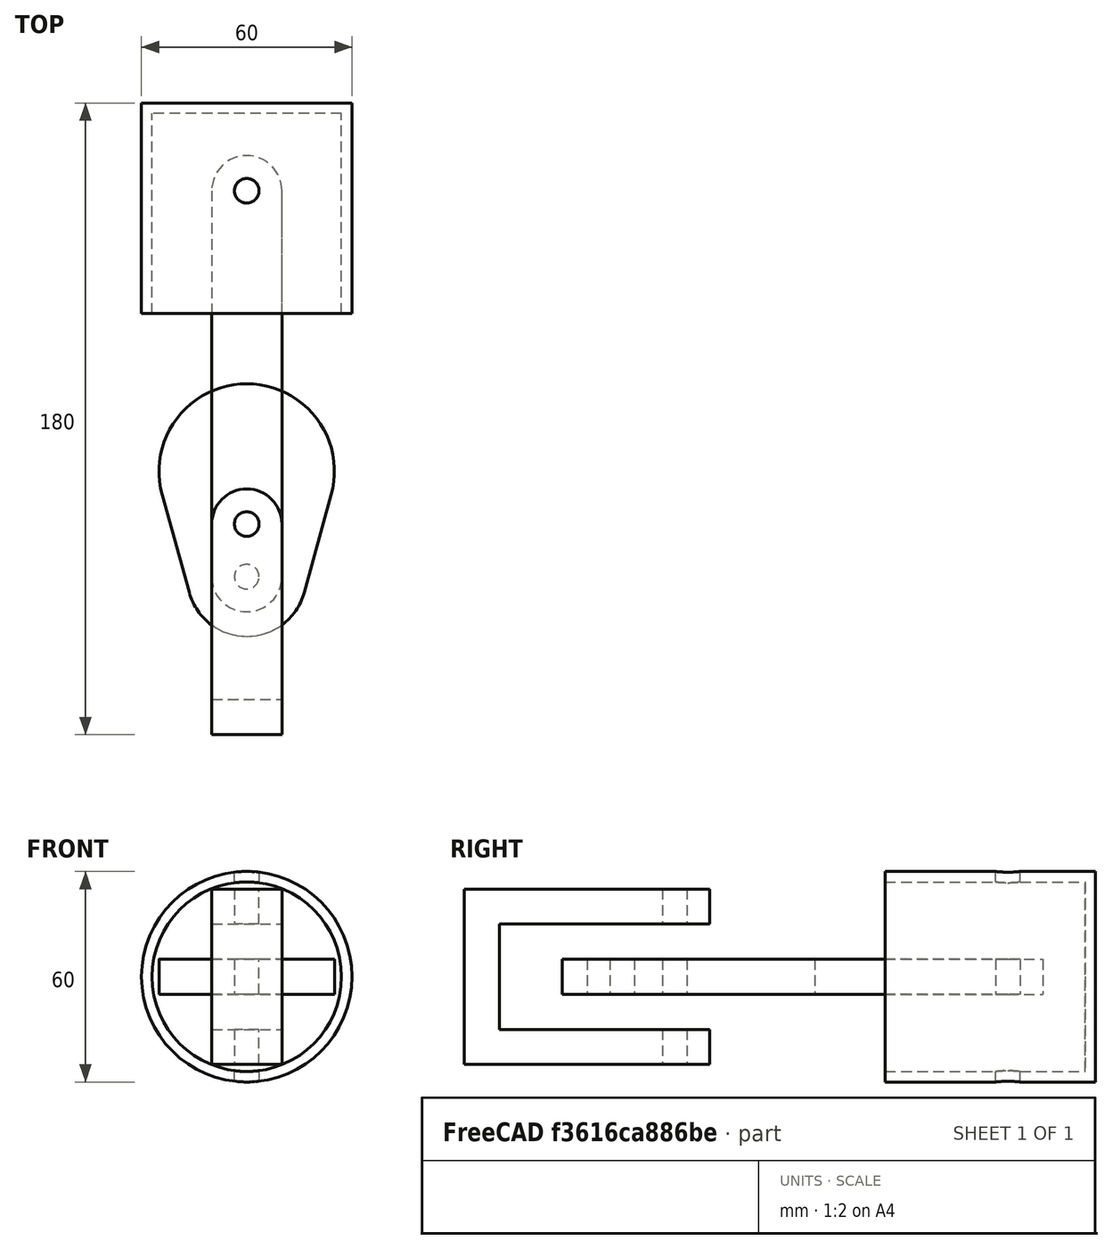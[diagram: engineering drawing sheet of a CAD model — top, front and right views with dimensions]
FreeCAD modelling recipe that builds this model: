
FCSTD DOCUMENT  (FreeCAD 1.0R39319 (Git))
Label: Piston_Head_Assembly
License: All rights reserved
LicenseURL: https://en.wikipedia.org/wiki/All_rights_reserved
objects: Sketcher::SketchObject×7, App::FeaturePython×6, PartDesign::SubShapeBinder×5, App::Link×5, PartDesign::Body×4, PartDesign::Pad×3, PartDesign::Pocket×2, PartDesign::Revolution×1, Assembly::JointGroup×1, Assembly::AssemblyObject×1
note: 41 computed .brp shape members not serialized (recipe doc carries the construction recipe); baked Part::Feature solids carry a one-line shape summary decoded from their .brp

FEATURE [Sketcher::SketchObject] Sketch  label="MasterSketch"
  ArcFitTolerance = 1e-06
  FullyConstrained = true
  MakeInternals = false
  sketch-geometry (19):
    g0: ArcOfCircle CenterX=2e-16 CenterY=55 CenterZ=0 NormalX=0 NormalY=0 NormalZ=1 AngleXU=0 Radius=10 StartAngle=4e-16 EndAngle=3.14159
    g1: ArcOfCircle CenterX=-2e-16 CenterY=-55 CenterZ=0 NormalX=0 NormalY=0 NormalZ=1 AngleXU=0 Radius=10 StartAngle=3.14159 EndAngle=6.28319
    g2: LineSegment StartX=10 StartY=55 StartZ=0 EndX=10 EndY=-55 EndZ=0
    g3: LineSegment StartX=-10 StartY=55 StartZ=0 EndX=-10 EndY=-55 EndZ=0
    g4: Circle CenterX=2e-16 CenterY=55 CenterZ=0 NormalX=0 NormalY=0 NormalZ=1 AngleXU=0 Radius=3.5
    g5: Circle CenterX=-2e-16 CenterY=-55 CenterZ=0 NormalX=0 NormalY=0 NormalZ=1 AngleXU=0 Radius=3.5
    g6: ArcOfCircle CenterX=0 CenterY=-25 CenterZ=0 NormalX=0 NormalY=0 NormalZ=1 AngleXU=0 Radius=25 StartAngle=6.01325 EndAngle=9.69471
    g7: ArcOfCircle CenterX=0 CenterY=-55 CenterZ=0 NormalX=0 NormalY=0 NormalZ=1 AngleXU=0 Radius=17 StartAngle=3.41153 EndAngle=6.01325
    g8: LineSegment StartX=-24.0947 StartY=-31.6667 StartZ=0 EndX=-16.3844 EndY=-59.5333 EndZ=0
    g9: LineSegment StartX=16.3844 StartY=-59.5333 StartZ=0 EndX=24.0947 EndY=-31.6667 EndZ=0
    g10: Circle CenterX=-7e-16 CenterY=-40 CenterZ=0 NormalX=0 NormalY=0 NormalZ=1 AngleXU=0 Radius=3.5
    g11: ArcOfCircle CenterX=-7e-16 CenterY=-40 CenterZ=0 NormalX=0 NormalY=0 NormalZ=1 AngleXU=0 Radius=10 StartAngle=0 EndAngle=3.14159
    g12: LineSegment StartX=-10 StartY=-40 StartZ=0 EndX=-10 EndY=-100 EndZ=0
    g13: LineSegment StartX=-10 StartY=-100 StartZ=0 EndX=10 EndY=-100 EndZ=0
    g14: LineSegment StartX=10 StartY=-100 StartZ=0 EndX=10 EndY=-40 EndZ=0
    g15: LineSegment StartX=-30 StartY=80 StartZ=0 EndX=-30 EndY=20 EndZ=0
    g16: LineSegment StartX=-30 StartY=20 StartZ=0 EndX=30 EndY=20 EndZ=0
    g17: LineSegment StartX=30 StartY=20 StartZ=0 EndX=30 EndY=80 EndZ=0
    g18: LineSegment StartX=30 StartY=80 StartZ=0 EndX=-30 EndY=80 EndZ=0
  constraints (47):
    c: Tangent(g0,g2) = 1.5708
    c: Tangent(g0,g3) = -1.5708
    c: Tangent(g1,g2) = 1.5708
    c: Tangent(g1,g3) = -1.5708
    c: Equal(g0,g1)
    c: Vertical(g3)
    c: Symmetric(g0,g1,g-1)
    c: DistanceY(g1,g0) = 110
    c: Radius(g0) = 10
    c: Coincident(g4,g0)
    c: Coincident(g5,g1)
    c: Equal(g4,g5)
    c: Diameter(g5) = 7
    c: PointOnObject(g6,g-2)
    c: PointOnObject(g7,g-2)
    c: Horizontal(g7,g7)
    c: Tangent(g8,g6) = -1.5708
    c: Tangent(g8,g7) = -1.5708
    c: Tangent(g9,g7) = -1.5708
    c: Tangent(g9,g6) = -1.5708
    c: Radius(g6) = 25
    c: Radius(g7) = 17
    c: DistanceY(g7,g6) = 30
    c: PointOnObject(g-1,g6)
    c: Coincident(g11,g10)
    c: Tangent(g11,g3) = -1.5708
    c: Tangent(g11,g2) = 1.5708
    c: Diameter(g10) = 7
    c: Tangent(g11,g12) = -1.5708
    c: Coincident(g12,g13)
    c: Horizontal(g13)
    c: Coincident(g13,g14)
    c: Coincident(g14,g11)
    c: Vertical(g14)
    c: Distance(g6,g10) = 15
    c: Distance(g10,g13) = 60
    c: Coincident(g15,g16)
    c: Coincident(g16,g17)
    c: Coincident(g17,g18)
    c: Coincident(g18,g15)
    c: Vertical(g15)
    c: Vertical(g17)
    c: Horizontal(g16)
    c: Distance(g15,g17) = 60
    c: Distance(g16,g18) = 60
    c: Symmetric(g15,g17,g-2)
    c: Distance(g-1,g16) = 20
FEATURE [PartDesign::SubShapeBinder] Binder
  BindCopyOnChange = 0
  BindMode = 0
  ClaimChildren = false
  Context = -> Body [Binder.]
  Fuse = false
  MakeFace = false
  OffsetFill = false
  OffsetIntersection = false
  OffsetJoinType = 0
  OffsetOpenResult = false
  PartialLoad = false
  Refine = true
  Relative = true
  Support = -> [Sketch]
  _Version = 2
FEATURE [Sketcher::SketchObject] Sketch001
  ArcFitTolerance = 1e-06
  AttachmentSupport = -> [XY_Plane]
  ExternalGeometry = -> [Binder]
  FullyConstrained = true
  MakeInternals = false
  MapMode = 5
  sketch-geometry (6):
    g0: LineSegment StartX=-10 StartY=55 StartZ=0 EndX=-10 EndY=-55 EndZ=0
    g1: ArcOfCircle CenterX=0 CenterY=-55 CenterZ=0 NormalX=0 NormalY=0 NormalZ=1 AngleXU=0 Radius=10 StartAngle=3.14159 EndAngle=6.28319
    g2: LineSegment StartX=10 StartY=-55 StartZ=0 EndX=10 EndY=55 EndZ=0
    g3: ArcOfCircle CenterX=-7.86e-14 CenterY=55 CenterZ=0 NormalX=0 NormalY=0 NormalZ=1 AngleXU=0 Radius=10 StartAngle=4e-16 EndAngle=3.14159
    g4: Circle CenterX=-7.86e-14 CenterY=55 CenterZ=0 NormalX=0 NormalY=0 NormalZ=1 AngleXU=0 Radius=3.5
    g5: Circle CenterX=0 CenterY=-55 CenterZ=0 NormalX=0 NormalY=0 NormalZ=1 AngleXU=0 Radius=3.5
  constraints (12):
    c: Coincident(g-4,g0)
    c: Coincident(g0,g-5)
    c: Tangent(g0,g1) = -1.5708
    c: Coincident(g1,g-6)
    c: Tangent(g1,g2) = -1.5708
    c: Tangent(g2,g3) = -1.5708
    c: Coincident(g3,g0)
    c: Coincident(g4,g3)
    c: Coincident(g5,g1)
    c: Equal(g5,g-7)
    c: Equal(g-8,g4)
    c: Equal(g3,g-3)
FEATURE [PartDesign::Pad] Pad
  Direction = (0,0,1)
  Length = 10
  Length2 = 10
  Midplane = true
  Profile = -> Sketch001
  ReferenceAxis = -> Sketch001 [N_Axis]
  Refine = true
  Suppressed = false
  Type = 0
FEATURE [PartDesign::Body] Body  label="Link"
  AllowCompound = false
  Group = -> [Binder,Sketch001,Pad]
  Origin = -> Origin
  Tip = -> Pad
FEATURE [PartDesign::SubShapeBinder] Binder001
  BindCopyOnChange = 0
  BindMode = 0
  ClaimChildren = false
  Context = -> Body001 [Binder001.]
  Fuse = false
  MakeFace = false
  OffsetFill = false
  OffsetIntersection = false
  OffsetJoinType = 0
  OffsetOpenResult = false
  PartialLoad = false
  Refine = true
  Relative = true
  Support = -> [Sketch]
  _Version = 2
FEATURE [Sketcher::SketchObject] Sketch002
  ArcFitTolerance = 1e-06
  AttachmentSupport = -> [XY_Plane001]
  ExternalGeometry = -> [Binder001]
  FullyConstrained = true
  MakeInternals = false
  MapMode = 5
  sketch-geometry (6):
    g0: LineSegment StartX=0 StartY=80 StartZ=0 EndX=-30 EndY=80 EndZ=0
    g1: LineSegment StartX=-30 StartY=80 StartZ=0 EndX=-30 EndY=20 EndZ=0
    g2: LineSegment StartX=-30 StartY=20 StartZ=0 EndX=-27 EndY=20 EndZ=0
    g3: LineSegment StartX=-27 StartY=20 StartZ=0 EndX=-27 EndY=77 EndZ=0
    g4: LineSegment StartX=-27 StartY=77 StartZ=0 EndX=0 EndY=77 EndZ=0
    g5: LineSegment StartX=0 StartY=77 StartZ=0 EndX=0 EndY=80 EndZ=0
  constraints (15):
    c: Symmetric(g-3,g-3,g0)
    c: Coincident(g0,g-4)
    c: Coincident(g0,g1)
    c: Coincident(g1,g-4)
    c: Coincident(g1,g2)
    c: PointOnObject(g2,g-5)
    c: Coincident(g2,g3)
    c: Vertical(g3)
    c: Coincident(g3,g4)
    c: PointOnObject(g4,g-2)
    c: Horizontal(g4)
    c: Coincident(g4,g5)
    c: Coincident(g5,g0)
    c: DistanceX(g2,g2) = 3
    c: DistanceY(g5,g5) = 3
FEATURE [PartDesign::Revolution] Revolution
  Angle = 360
  Angle2 = 60
  Axis = (1e-16,1,-1e-16)
  Base = (0,0,0)
  Midplane = true
  Profile = -> Sketch002
  ReferenceAxis = -> Y_Axis001
  Refine = true
  Suppressed = false
  Type = 0
FEATURE [Sketcher::SketchObject] Sketch003
  ArcFitTolerance = 1e-06
  AttachmentSupport = -> [XY_Plane001]
  ExternalGeometry = -> [Binder001]
  FullyConstrained = true
  MakeInternals = false
  MapMode = 5
  sketch-geometry (1):
    g0: Circle CenterX=0 CenterY=55 CenterZ=0 NormalX=0 NormalY=0 NormalZ=1 AngleXU=0 Radius=3.5
  constraints (2):
    c: Coincident(g0,g-3)
    c: Equal(g0,g-3)
FEATURE [PartDesign::Pocket] Pocket
  BaseFeature = -> Revolution
  Direction = (0,0,-1)
  Length = 52
  Length2 = 5
  Midplane = true
  Profile = -> Sketch003
  ReferenceAxis = -> Sketch003 [N_Axis]
  Refine = true
  Suppressed = false
  Type = 1
FEATURE [PartDesign::Body] Body001  label="Piston_Head"
  AllowCompound = false
  Group = -> [Binder001,Sketch002,Revolution,Sketch003,Pocket]
  Origin = -> Origin001
  Tip = -> Pocket
FEATURE [PartDesign::SubShapeBinder] Binder002
  BindCopyOnChange = 0
  BindMode = 0
  ClaimChildren = false
  Context = -> Body002 [Binder002.]
  Fuse = false
  MakeFace = false
  OffsetFill = false
  OffsetIntersection = false
  OffsetJoinType = 0
  OffsetOpenResult = false
  PartialLoad = false
  Refine = true
  Relative = true
  Support = -> [Sketch]
  _Version = 2
FEATURE [Sketcher::SketchObject] Sketch004
  ArcFitTolerance = 1e-06
  AttachmentSupport = -> [XY_Plane002]
  ExternalGeometry = -> [Binder002]
  FullyConstrained = true
  MakeInternals = false
  MapMode = 5
  sketch-geometry (6):
    g0: ArcOfCircle CenterX=0 CenterY=-25 CenterZ=0 NormalX=0 NormalY=0 NormalZ=1 AngleXU=0 Radius=25 StartAngle=6.01325 EndAngle=9.69471
    g1: ArcOfCircle CenterX=0 CenterY=-55 CenterZ=0 NormalX=0 NormalY=0 NormalZ=1 AngleXU=0 Radius=17 StartAngle=3.41153 EndAngle=6.01325
    g2: LineSegment StartX=-24.0947 StartY=-31.6667 StartZ=0 EndX=-16.3844 EndY=-59.5333 EndZ=0
    g3: LineSegment StartX=24.0947 StartY=-31.6667 StartZ=0 EndX=16.3844 EndY=-59.5333 EndZ=0
    g4: Circle CenterX=0 CenterY=-40 CenterZ=0 NormalX=0 NormalY=0 NormalZ=1 AngleXU=0 Radius=3.5
    g5: Circle CenterX=0 CenterY=-55 CenterZ=0 NormalX=0 NormalY=0 NormalZ=1 AngleXU=0 Radius=3.5
  constraints (14):
    c: Coincident(g0,g-3)
    c: Coincident(g0,g-5)
    c: Coincident(g1,g-6)
    c: Coincident(g1,g-6)
    c: Horizontal(g1,g1)
    c: Horizontal(g0,g0)
    c: Coincident(g2,g0)
    c: Coincident(g2,g1)
    c: Coincident(g3,g0)
    c: Coincident(g3,g1)
    c: Coincident(g4,g-7)
    c: Coincident(g5,g1)
    c: Equal(g4,g-7)
    c: Equal(g5,g-8)
FEATURE [PartDesign::SubShapeBinder] Binder003
  BindCopyOnChange = 0
  BindMode = 0
  ClaimChildren = false
  Context = -> Body003 [Binder003.]
  Fuse = false
  MakeFace = false
  OffsetFill = false
  OffsetIntersection = false
  OffsetJoinType = 0
  OffsetOpenResult = false
  PartialLoad = false
  Refine = true
  Relative = true
  Support = -> [Sketch]
  _Version = 2
FEATURE [Sketcher::SketchObject] Sketch005
  ArcFitTolerance = 1e-06
  AttachmentSupport = -> [XY_Plane003]
  ExternalGeometry = -> [Binder003]
  FullyConstrained = true
  MakeInternals = false
  MapMode = 5
  sketch-geometry (5):
    g0: LineSegment StartX=-10 StartY=-40 StartZ=0 EndX=-10 EndY=-100 EndZ=0
    g1: LineSegment StartX=-10 StartY=-100 StartZ=0 EndX=10 EndY=-100 EndZ=0
    g2: LineSegment StartX=10 StartY=-100 StartZ=0 EndX=10 EndY=-40 EndZ=0
    g3: ArcOfCircle CenterX=8e-16 CenterY=-40 CenterZ=0 NormalX=0 NormalY=0 NormalZ=1 AngleXU=0 Radius=10 StartAngle=0 EndAngle=3.14159
    g4: Circle CenterX=8e-16 CenterY=-40 CenterZ=0 NormalX=0 NormalY=0 NormalZ=1 AngleXU=0 Radius=3.5
  constraints (12):
    c: Coincident(g0,g1)
    c: Coincident(g1,g-7)
    c: Coincident(g1,g2)
    c: Coincident(g2,g-5)
    c: Tangent(g2,g3) = -1.5708
    c: Coincident(g3,g0)
    c: Equal(g0,g-6)
    c: Horizontal(g2,g0)
    c: Equal(g-7,g1)
    c: Coincident(g4,g3)
    c: Equal(g4,g-4)
    c: Equal(g-3,g3)
FEATURE [PartDesign::Pad] Pad002
  Direction = (0,0,1)
  Length = 50
  Length2 = 10
  Midplane = true
  Profile = -> Sketch005
  ReferenceAxis = -> Sketch005 [N_Axis]
  Refine = true
  Suppressed = false
  Type = 0
FEATURE [PartDesign::SubShapeBinder] Binder004
  BindCopyOnChange = 0
  BindMode = 0
  ClaimChildren = false
  Context = -> Body003 [Binder004.]
  Fuse = false
  MakeFace = false
  OffsetFill = false
  OffsetIntersection = false
  OffsetJoinType = 0
  OffsetOpenResult = false
  PartialLoad = false
  Refine = true
  Relative = true
  Support = -> [Body002]
  _Version = 2
FEATURE [Sketcher::SketchObject] Sketch006
  ArcFitTolerance = 1e-06
  AttachmentSupport = -> [Pad002]
  ExternalGeometry = -> [Pad002]
  FullyConstrained = true
  MakeInternals = false
  MapMode = 5
  Placement = pos=(-10,-3e-16,0) rot=(0.57735,-0.57735,-0.57735;2.0944rad)
  sketch-geometry (4):
    g0: LineSegment StartX=0 StartY=15 StartZ=0 EndX=0 EndY=-15 EndZ=0
    g1: LineSegment StartX=0 StartY=-15 StartZ=0 EndX=90 EndY=-15 EndZ=0
    g2: LineSegment StartX=90 StartY=-15 StartZ=0 EndX=90 EndY=15 EndZ=0
    g3: LineSegment StartX=90 StartY=15 StartZ=0 EndX=0 EndY=15 EndZ=0
  constraints (11):
    c: Coincident(g0,g1)
    c: Coincident(g1,g2)
    c: Coincident(g2,g3)
    c: Coincident(g3,g0)
    c: Vertical(g2)
    c: Horizontal(g1)
    c: Horizontal(g3)
    c: PointOnObject(g0,g-2)
    c: Symmetric(g0,g0,g-1)
    c: DistanceY(g2,g2) = 30
    c: Distance(g-3,g2) = 10
FEATURE [PartDesign::Pocket] Pocket001
  BaseFeature = -> Pad002
  Direction = (1,0,0)
  Length = 5
  Length2 = 5
  Profile = -> Sketch006
  ReferenceAxis = -> Sketch006 [N_Axis]
  Refine = true
  Suppressed = false
  Type = 1
FEATURE [PartDesign::Body] Body003  label="Mount"
  AllowCompound = false
  Group = -> [Binder003,Sketch005,Pad002,Binder004,Sketch006,Pocket001]
  Origin = -> Origin003
  Tip = -> Pocket001
FEATURE [App::Link] Mount  label="Mount001"
  LinkedObject = -> Body003
FEATURE [App::FeaturePython] GroundedJoint  # Assembly grounded joint (typed FeaturePython)
  ObjectToGround = -> Mount
FEATURE [App::Link] Crank  label="Crank001"
  LinkPlacement = pos=(-37.7776,-53.1511,-10.0102) rot=(0.000277,-0.00039,1;1.9057rad)
  LinkedObject = -> Body002
  Placement = pos=(-37.7776,-53.1511,-10.0102) rot=(0.000277,-0.00039,1;1.9057rad)
FEATURE [App::Link] Link  label="Link001"
  LinkPlacement = pos=(7.08331,19.4605,0.0463491) rot=(-0.064528,0.997916,0.000389;3.14154rad)
  LinkedObject = -> Body
  Placement = pos=(7.08331,19.4605,0.0463491) rot=(-0.064528,0.997916,0.000389;3.14154rad)
FEATURE [App::FeaturePython] Joint002  label="Revolute001"  # Assembly joint (typed FeaturePython)
  Activated = true
  AngleMax = 0
  AngleMin = 0
  Detach1 = false
  Detach2 = false
  Distance = 0
  Distance2 = 0
  EnableAngleMax = false
  EnableAngleMin = false
  EnableLengthMax = false
  EnableLengthMin = false
  JointType = 1 (Revolute)
  LengthMax = 0
  LengthMin = 0
  Placement1 = pos=(0,-55,5) rot=(0,0,1;0rad)
  Placement2 = pos=(-1.42e-14,-55,5) rot=(0,0,1;0rad)
  Reference1 = -> Assembly [Link.Edge15,Link.Edge15]
  Reference2 = -> Assembly [Crank.Edge15,Crank.Edge15]
FEATURE [App::Link] Piston_Head  label="Piston_Head001"
  LinkPlacement = pos=(3.8e-15,19.0025,-0.0623533) rot=(1,0,0;0.000779rad)
  LinkedObject = -> Body001
  Placement = pos=(3.8e-15,19.0025,-0.0623533) rot=(1,0,0;0.000779rad)
FEATURE [App::FeaturePython] Joint003  label="Revolute002"  # Assembly joint (typed FeaturePython)
  Activated = true
  AngleMax = 0
  AngleMin = 0
  Detach1 = false
  Detach2 = false
  Distance = 0
  Distance2 = 0
  EnableAngleMax = false
  EnableAngleMin = false
  EnableLengthMax = false
  EnableLengthMin = false
  JointType = 1 (Revolute)
  LengthMax = 0
  LengthMin = 0
  Offset2 = pos=(0,0,28.5) rot=(0,0,1;0rad)
  Placement1 = pos=(-7.46e-14,55,-3e-16) rot=(0,0,1;0rad)
  Placement2 = pos=(0,55,0.108345) rot=(0,0,1;0rad)
  Reference1 = -> Assembly [Link.Face6,Link.Face6]
  Reference2 = -> Assembly [Piston_Head.Face5,Piston_Head.Face5]
FEATURE [App::FeaturePython] Joint004  label="Slider"  # Assembly joint (typed FeaturePython)
  Activated = true
  AngleMax = 0
  AngleMin = 0
  Detach1 = false
  Detach2 = false
  Distance = 0
  Distance2 = 0
  EnableAngleMax = false
  EnableAngleMin = false
  EnableLengthMax = false
  EnableLengthMin = false
  JointType = 3 (Slider)
  LengthMax = 0
  LengthMin = 0
  Placement1 = pos=(-1.4e-15,-90,-3e-16) rot=(0.57735,-0.57735,0.57735;2.0944rad)
  Placement2 = pos=(3.6e-15,80,-4.3e-15) rot=(0,0.707107,-0.707107;3.14159rad)
  Reference1 = -> Assembly [Mount.Face7,Mount.Face7]
  Reference2 = -> Assembly [Piston_Head.Face1,Piston_Head.Face1]
FEATURE [PartDesign::Pad] Pad001
  Direction = (0,0,1)
  Length = 10
  Length2 = 10
  Midplane = true
  Profile = -> Sketch004
  ReferenceAxis = -> Sketch004 [N_Axis]
  Refine = true
  Suppressed = false
  Type = 0
FEATURE [PartDesign::Body] Body002  label="Crank"
  AllowCompound = false
  Group = -> [Binder002,Sketch004,Pad001]
  Origin = -> Origin002
  Tip = -> Pad001
FEATURE [App::FeaturePython] Joint  label="Revolute"  # Assembly joint (typed FeaturePython)
  Activated = true
  AngleMax = 0
  AngleMin = 0
  Detach1 = false
  Detach2 = false
  Distance = 0
  Distance2 = 0
  EnableAngleMax = false
  EnableAngleMin = false
  EnableLengthMax = false
  EnableLengthMin = false
  JointType = 1 (Revolute)
  LengthMax = 0
  LengthMin = 0
  Placement1 = pos=(-7.1e-15,-40,-5) rot=(0,0,1;0rad)
  Placement2 = pos=(7e-16,-40,-15) rot=(1,0,0;3.14159rad)
  Reference1 = -> Assembly [Crank.Edge17,Crank.Edge17]
  Reference2 = -> Assembly [Mount.Edge27,Mount.Edge27]
FEATURE [App::Link] Crank001  label="Crank002"
  LinkPlacement = pos=(-37.7776,-53.1667,9.98975) rot=(0.000277,-0.00039,1;1.9057rad)
  LinkedObject = -> Body002
  Placement = pos=(-37.7776,-53.1667,9.98975) rot=(0.000277,-0.00039,1;1.9057rad)
FEATURE [App::FeaturePython] Joint005  label="Fixed"  # Assembly joint (typed FeaturePython)
  Activated = true
  AngleMax = 0
  AngleMin = 0
  Detach1 = false
  Detach2 = false
  Distance = 0
  Distance2 = 0
  EnableAngleMax = false
  EnableAngleMin = false
  EnableLengthMax = false
  EnableLengthMin = false
  JointType = 0 (Fixed)
  LengthMax = 0
  LengthMin = 0
  Offset2 = pos=(0,0,-10) rot=(0,0,1;0rad)
  Placement1 = pos=(24.0947,-31.6667,5) rot=(0,0,1;0rad)
  Placement2 = pos=(24.0947,-31.6667,-15) rot=(0,0,1;0rad)
  Reference1 = -> Assembly [Crank.Face8,Crank.Vertex2]
  Reference2 = -> Assembly [Crank001.Face7,Crank001.Vertex1]
FEATURE [Assembly::JointGroup] Joints
  Group = -> [GroundedJoint,Joint002,Joint003,Joint004,Joint,Joint005]
FEATURE [Assembly::AssemblyObject] Assembly
  Group = -> [Joints,Mount,GroundedJoint,Crank,Link,Joint002,Piston_Head,Joint003,Joint004,Joint,Crank001,Joint005]
  Origin = -> Origin004
  Type = Assembly
